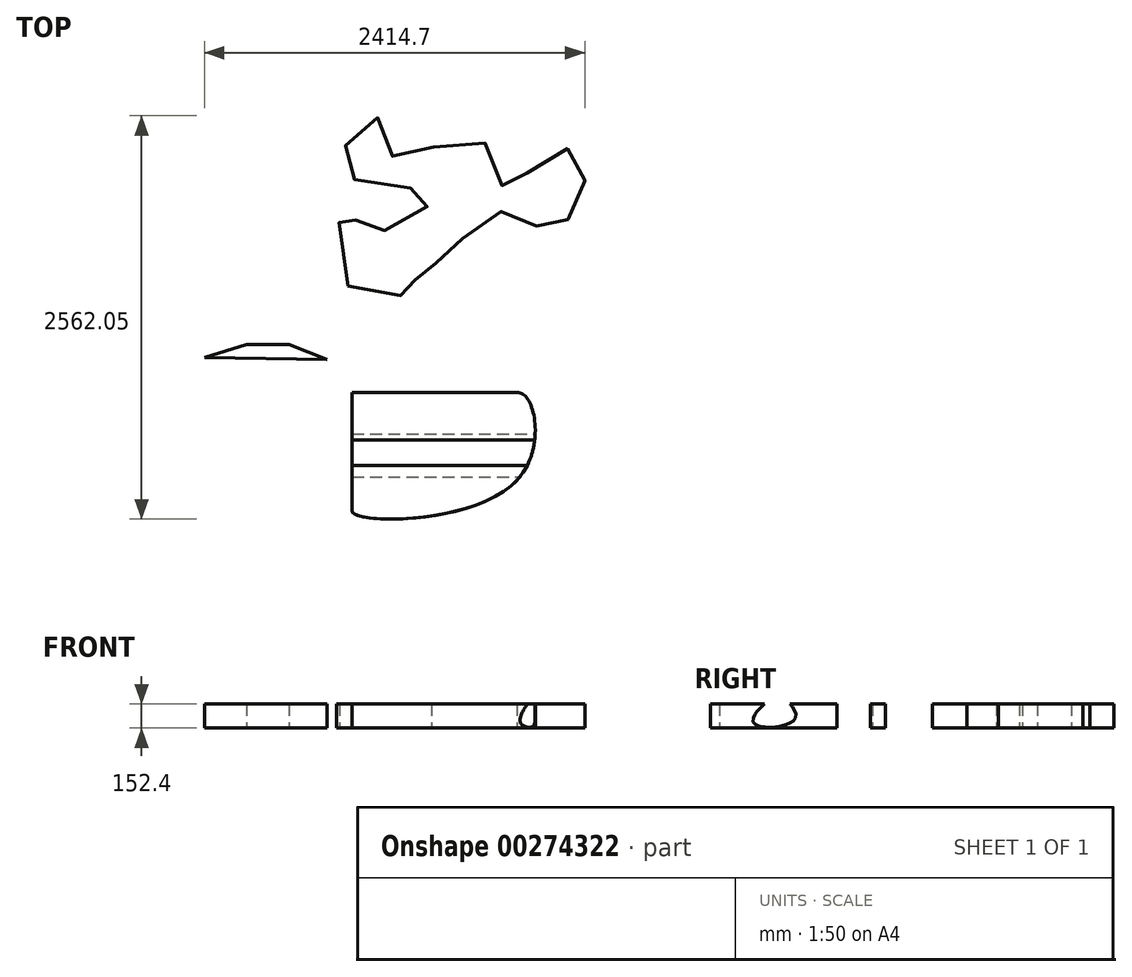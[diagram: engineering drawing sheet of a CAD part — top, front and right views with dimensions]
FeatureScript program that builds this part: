
annotation { "Feature Type Name" : "Feature", "Feature Type Description" : "" }
export const myFeature = defineFeature(function(context is Context, id is Id, definition is map)
    precondition{}
    {
        {
            var Q0;
            Q0=qCreatedBy(makeId("Top.planeOp"),FACE);
            var sketch = newSketch(context, id + "F0", { "sketchPlane" : qUnion([Q0])});
            skLineSegment(sketch, "E0", {"start": v(78.9, 111.31) * mm, "end": v(1126.65, 111.31) * mm});
            skLineSegment(sketch, "E1", {"start": v(78.9, 111.31) * mm, "end": v(78.9, 42.38) * mm});
            skLineSegment(sketch, "E2", {"start": v(78.9, 42.38) * mm, "end": v(78.9, -636.58) * mm});
            skLineSegment(sketch, "E3", {"start": v(-858.54, 335.34) * mm, "end": v(-593.16, 418.05) * mm});
            skLineSegment(sketch, "E4", {"start": v(-593.16, 418.05) * mm, "end": v(-320.89, 418.05) * mm});
            skLineSegment(sketch, "E5", {"start": v(-320.89, 418.05) * mm, "end": v(-79.63, 321.55) * mm});
            skLineSegment(sketch, "E6", {"start": v(-858.54, 335.34) * mm, "end": v(-79.63, 321.55) * mm});
            skFitSpline(sketch, "E7", {"points": [v(1126.65, 111.31) * mm, v(846.12, -394.81) * mm, v(811.65, -412.04) * mm, v(78.9, -636.58) * mm, v(1126.65, -443.06) * mm, v(1126.65, 111.31) * mm]});
            skFitSpline(sketch, "E8", {"points": [v(53.03, 787.94) * mm, v(442.66, 736.65) * mm, v(460.34, 744.52) * mm, v(516.34, 917.91) * mm, v(643.17, 942.26) * mm, v(826.7, 1148.34) * mm, v(1128.14, 1258.42) * mm, v(1321.73, 1135.92) * mm, v(1521.91, 1321.33) * mm, v(1533.86, 1559.38) * mm, v(1362.82, 1663.82) * mm, v(1055.17, 1382.44) * mm, v(972.23, 1654.5) * mm, v(584.91, 1666.7) * mm, v(322.03, 1625.93) * mm, v(221.09, 1869.92) * mm, v(0, 1555) * mm, v(263.48, 1439.37) * mm, v(583.88, 1341.21) * mm, v(336.46, 1166.89) * mm, v(144.7, 1145.75) * mm, v(36.28, 1286.09) * mm, v(53.03, 787.94) * mm]});
            skSolve(sketch);
        }
        {
            var Q0;
            Q0 = qSketchRegion(id + "F0", true);
            extrude(context, id + "F1", {"entities" : qUnion([Q0]), "depth" : 152.4 * mm});
        }
        {
            var Q0;
            Q0=makeQuery(id+"F1.opExtrude","SWEPT_FACE",FACE,{"disambiguationData":[OSD([sQuery(id+"F0.wireOp",EDGE,"E1"),sQuery(id+"F0.wireOp",EDGE,"E2")])]});
            var sketch = newSketch(context, id + "F2", { "sketchPlane" : qUnion([Q0])});
            skFitSpline(sketch, "E9", {"points": [v(153.76, 61.16) * mm, v(236.8, 188.8) * mm, v(281.4, 188.8) * mm, v(372.13, 133.43) * mm, v(412.1, 25.79) * mm, v(153.76, 61.16) * mm]});
            skSolve(sketch);
        }
        {
            var Q0;
            Q0 = qSketchRegion(id + "F2", true);
            extrude(context, id + "F3", {"entities" : qUnion([Q0]), "operationType" : NewBodyOperationType.REMOVE, "endBound" : BoundingType.THROUGH_ALL, "oppositeDirection" : true, "depth" : 25.4 * mm});
        }
    });
